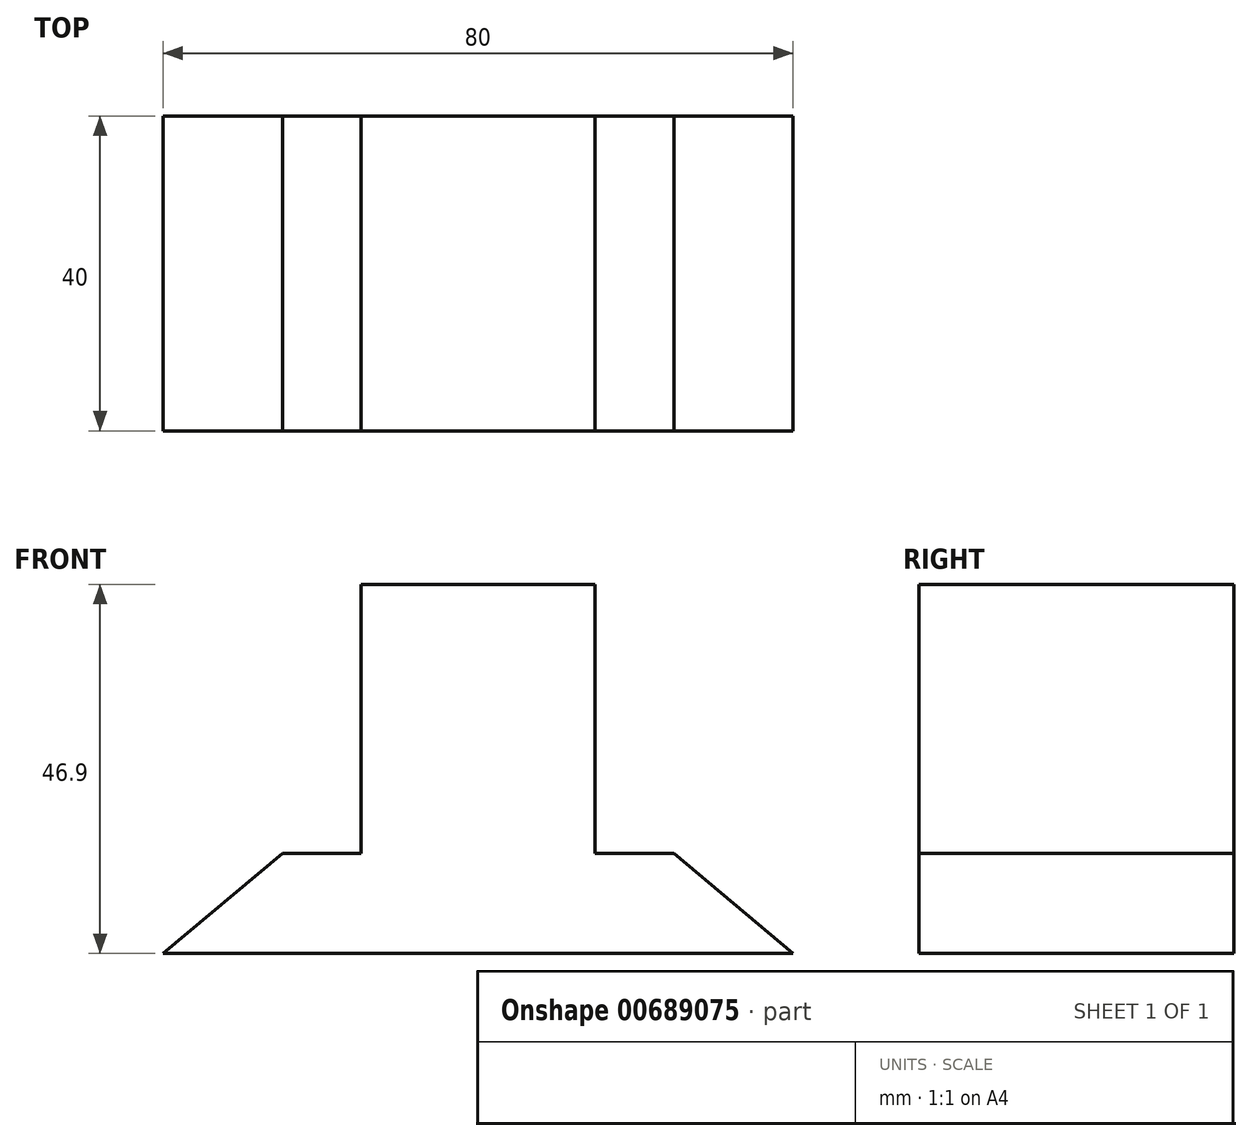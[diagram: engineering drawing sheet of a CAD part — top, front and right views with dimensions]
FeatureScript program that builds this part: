
annotation { "Feature Type Name" : "Feature", "Feature Type Description" : "" }
export const myFeature = defineFeature(function(context is Context, id is Id, definition is map)
    precondition{}
    {
        {
            var Q0;
            Q0=qCreatedBy(makeId("Front.planeOp"),FACE);
            var sketch = newSketch(context, id + "F0", { "sketchPlane" : qUnion([Q0])});
            skLineSegment(sketch, "E0", {"start": v(-54.86, -46.9) * mm, "end": v(25.14, -46.9) * mm});
            skLineSegment(sketch, "E1", {"start": v(25.14, -46.9) * mm, "end": v(10, -34.2) * mm});
            skLineSegment(sketch, "E2", {"start": v(10, -34.2) * mm, "end": v(0, -34.2) * mm});
            skLineSegment(sketch, "E3", {"start": v(0, -34.2) * mm, "end": v(0, 0) * mm});
            skLineSegment(sketch, "E4", {"start": v(0, 0) * mm, "end": v(-29.72, 0) * mm});
            skLineSegment(sketch, "E5", {"start": v(-29.72, 0) * mm, "end": v(-29.72, -34.2) * mm});
            skLineSegment(sketch, "E6", {"start": v(-29.72, -34.2) * mm, "end": v(-39.72, -34.2) * mm});
            skLineSegment(sketch, "E7", {"start": v(-39.72, -34.2) * mm, "end": v(-54.86, -46.9) * mm});
            skSolve(sketch);
        }
        {
            var Q0;
            Q0=makeQuery(id+"F0.imprint","IMPRINT",FACE,{"disambiguationData":[TD([[makeQuery(id+"F0.imprint","IMPRINT",EDGE,{"derivedFrom":sQuery(id+"F0.wireOp",EDGE,"E0")}),1.0]])]});
            extrude(context, id + "F1", {"entities" : qUnion([Q0]), "depth" : 40 * mm, "offsetDistance" : 25.4 * mm});
        }
    });
